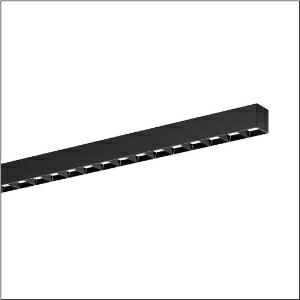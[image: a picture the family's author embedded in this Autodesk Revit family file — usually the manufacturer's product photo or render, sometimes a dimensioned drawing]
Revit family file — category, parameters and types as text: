
# Revit family: silica_r__21_51mx22dc3abb_349a
name_source: partatom
category: Lighting Fixtures
units: mm (PartAtom-declared; Revit-internal decimal feet)

## family parameters
Cut with Voids When Loaded = No
Host = Face
Light Source = No
Part Type = Normal
Room Calculation Point = No
Round Connector Dimension = Use Diameter
Shared = No

## types (1)
- --- (1 x LED, 10800 lm, 69.2 W, 3000K)
    Apparent Load = 69 VA
    CIE Flux Codes = 86 100 100 100 100
    Color Rendering = 80
    Color Temperature = 3000K
    Default Elevation = 1800 mm
    Description = Silica® 21, office luminaire, primary light control with darklight reflector, of PMMA, black, CAT 2 (L<= 3000cd/m²), light emission: direct distribution, primary light characteristic: symmetric, installation type: surface-mounted, LED, rated luminous flux: 10.800lm, luminous efficacy: 156lm/W, light colour: 830, colour temperature: 3000K, with terminal, 3+2-pole, max. 2.5mm², mains connection: 220..240V, AC, 50/60Hz, rated input power: 69.2W, luminaire housing, of aluminium, jet black (RAL 9005), length: 3.004mm, width: 53mm, height: 53mm, protection rating (complete): IP20, insulation class (complete): insulation class I (protective earthing), certification: CE, permissible operating ambient temperature: 0..+35°C, standard: EN 50419, packaging unit: 1 piece
    Height = 0 mm  [stored 0 ft]
    Lamp = 1 x LED
    Lamp Light Flux = 10800 lm
    Lamp Power = 69.2 W
    Lamp count = 1
    Length = 3004 mm
    Luminous efficacy = 156 lm/W
    Manufacturer = Siteco
    ModVariant = No
    Model = 51MX22DC3ABB
    Mounting Place = Ceiling
    Mounting Type = Recessed
    Number of Poles = 1
    OnlyDefault = Yes
    Power Factor = 1
    Product Name = Silica® 21
    Product group = office luminaire | ceiling recessed
    ProductGroupID = 400
    Protection Class = Protection class I
    Protection Degree = IP 20
    RLX_Detail_Level = 1
    RLX_Emergency_Light_Flux = 0 lm
    RLX_Emergency_Type = 0
    RLX_Emergency_Type_DB = No
    RlxData = <blob elided: 64517 chars, md5=60e44d48>
    Socket = socket
    Standby Power = 0 W
    System Light Flux = 10800 lm
    System Power = 69 W
    Type Comments = factory setting: luminous flux: 100 % | dim-lin: 254 | 392 mA
    Type Image = l_1335908.jpg
    URL = http://relux.com
    VarID = @adj_094847
    Voltage = 0 V
    Weight = 0.00 kg
    Width = 53 mm

note: [stored X ft] marks values corroborated as IEEE doubles in the binary element streams (Revit-internal decimal feet)

## geometry (parser evidence)
native form markers: Blend x4, Sweep x10
no freeform markers — native parametric forms only
